# Revit family: Workstations-Multi_Level-Teknion-B_ATHP_HA_Tapered_Peninsula_High_Secondary_Desk_Bevel_Post_Leg-R2018
name_source: partatom
category: Furniture
revit_build: Autodesk Revit 2018 (Build: 20190510_1515(x64)
units: mm (PartAtom-declared; Revit-internal decimal feet)

## family parameters
Always vertical = Yes
Cut with Voids When Loaded = No
OmniClass Number = 23.40.20.00
OmniClass Title = General Furniture and Specialties
Room Calculation Point = No
Shared = Yes
Work Plane-Based = No

## types (6) — shared parameters
Assembly Code = E2020200
Manufacturer = Teknion
Manufacturer Fax = 416.661.4586
Part Number = B_ATHP
Product Documentation Link = https://www.teknion.com
Product Documentation Link #2 = https://www.teknion.com
Product Documentation Link #3 = https://www.teknion.com
Product Documentation Link #4 = https://www.teknion.com
Product Documentation Link #5 = https://www.teknion.com
Product Line = Expansion Casegoods
Product Page URL = https://www.teknion.com
Series = Expansion Casegoods
Sustainability Data = https://www.teknion.com
URL = www.teknion.com
Unit Weight URL = http://www.teknion.com
Warranty = http://www.teknion.com

## per-type parameters (varying)
| type | Depth | Description | Leg Offset | Model | Worksurface Thickness |
| 1-3/16" Worksurface Thickness, Extended Range - 29" to 48", 46" Depth | 45.76 " | Height-Adjustable Tapered Peninsula – High Secondary Desk – Bevel post Leg,1-3/16" Worksurface Thickness, Extended Range - 29" to 48", 46" Depth | 25.373 " | BMATHPE46____ | 1.189 " |
| 1-9/16" Worksurface Thickness, Extended Range - 29" to 48", 46" Depth | 45.76 " | Height-Adjustable Tapered Peninsula – High Secondary Desk – Bevel post Leg,1-9/16" Worksurface Thickness, Extended Range - 29" to 48", 46" Depth | 25.373 " | BXATHPE46____ | 1.555 " |
| 1-3/16" Worksurface Thickness, Extended Range - 29" to 48", 41" Depth | 41 " | Height-Adjustable Tapered Peninsula – High Secondary Desk – Bevel post Leg,1-3/16" Worksurface Thickness, Extended Range - 29" to 48", 41" Depth | 28.855 " | BMATHPE41____ | 1.189 " |
| 1-3/16" Worksurface Thickness, Extended Range - 29" to 48", 35" Depth | 35 " | Height-Adjustable Tapered Peninsula – High Secondary Desk – Bevel post Leg,1-3/16" Worksurface Thickness, Extended Range - 29" to 48", 35" Depth | 22.885 " | BMATHPE35____ | 1.189 " |
| 1-9/16" Worksurface Thickness, Extended Range - 29" to 48", 41" Depth | 41 " | Height-Adjustable Tapered Peninsula – High Secondary Desk – Bevel post Leg,1-9/16" Worksurface Thickness, Extended Range - 29" to 48", 41" Depth | 28.855 " | BXATHPE41____ | 1.555 " |
| 1-9/16" Worksurface Thickness, Extended Range - 29" to 48", 35" Depth | 35 " | Height-Adjustable Tapered Peninsula – High Secondary Desk – Bevel post Leg,1-9/16" Worksurface Thickness, Extended Range - 29" to 48", 35" Depth | 22.885 " | BXATHPE35____ | 1.555 " |

## geometry (parser evidence)
native form markers: Sweep x4
no freeform markers — native parametric forms only
